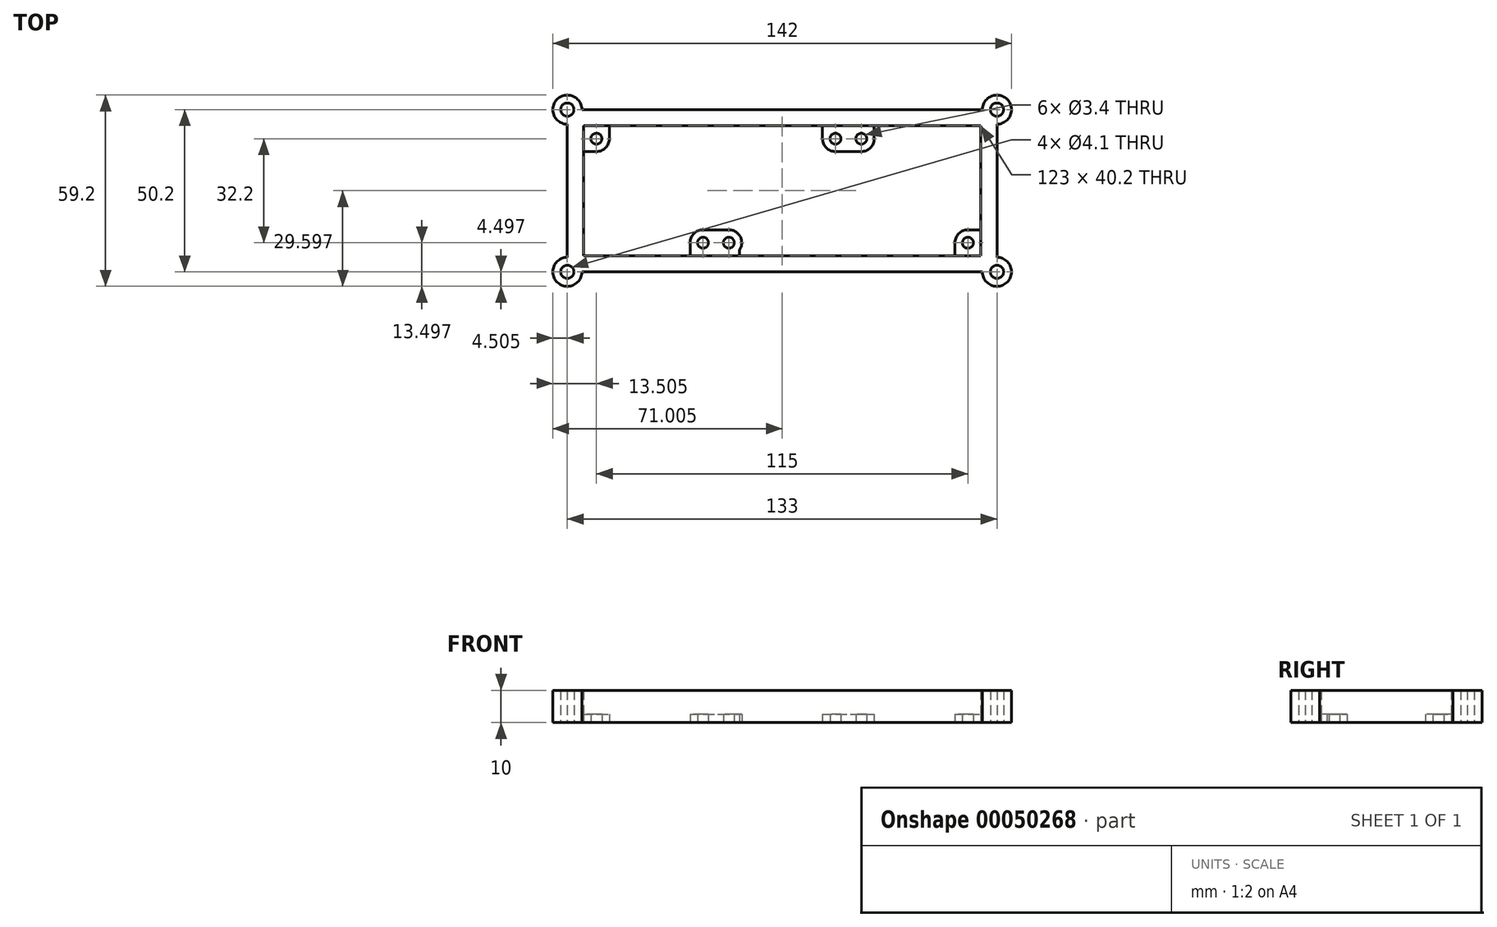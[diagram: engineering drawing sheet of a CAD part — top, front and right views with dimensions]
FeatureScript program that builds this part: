
annotation { "Feature Type Name" : "Feature", "Feature Type Description" : "" }
export const myFeature = defineFeature(function(context is Context, id is Id, definition is map)
    precondition{}
    {
        {
            var Q0;
            Q0=qCreatedBy(makeId("Top.planeOp"),FACE);
            var sketch = newSketch(context, id + "F0", { "sketchPlane" : qUnion([Q0])});
            skLineSegment(sketch, "E0.bottom", {"start": v(-53.3, 36.32) * mm, "end": v(79.7, 36.32) * mm});
            skLineSegment(sketch, "E0.top", {"start": v(-53.3, -13.88) * mm, "end": v(79.7, -13.88) * mm});
            skLineSegment(sketch, "E0.left", {"start": v(-53.3, 36.32) * mm, "end": v(-53.3, -13.88) * mm});
            skLineSegment(sketch, "E0.right", {"start": v(79.7, 36.32) * mm, "end": v(79.7, -13.88) * mm});
            skLineSegment(sketch, "E1.bottom", {"start": v(-48.3, 31.32) * mm, "end": v(74.7, 31.32) * mm});
            skLineSegment(sketch, "E1.top", {"start": v(-48.3, -8.88) * mm, "end": v(74.7, -8.88) * mm});
            skLineSegment(sketch, "E1.left", {"start": v(-48.3, 31.32) * mm, "end": v(-48.3, -8.88) * mm});
            skLineSegment(sketch, "E1.right", {"start": v(74.7, 31.32) * mm, "end": v(74.7, -8.88) * mm});
            skCircle(sketch, "E2", {"center": v(-44.3, 27.32) * mm, "radius": 4 * mm});
            skCircle(sketch, "E3", {"center": v(-3.3, -4.88) * mm, "radius": 4 * mm});
            skCircle(sketch, "E4", {"center": v(-11.3, -4.88) * mm, "radius": 4 * mm});
            skCircle(sketch, "E5", {"center": v(29.7, 27.32) * mm, "radius": 4 * mm});
            skCircle(sketch, "E6", {"center": v(37.7, 27.32) * mm, "radius": 4 * mm});
            skCircle(sketch, "E7", {"center": v(70.7, -4.88) * mm, "radius": 4 * mm});
            skLineSegment(sketch, "E8", {"start": v(29.7, 23.32) * mm, "end": v(37.7, 23.32) * mm});
            skLineSegment(sketch, "E9", {"start": v(-11.3, -0.88) * mm, "end": v(-3.3, -0.88) * mm});
            skLineSegment(sketch, "E10", {"start": v(-44.3, 23.32) * mm, "end": v(-48.3, 23.32) * mm});
            skLineSegment(sketch, "E11", {"start": v(-40.3, 27.32) * mm, "end": v(-40.3, 31.32) * mm});
            skLineSegment(sketch, "E12", {"start": v(25.7, 27.32) * mm, "end": v(25.7, 31.32) * mm});
            skLineSegment(sketch, "E13", {"start": v(41.7, 27.32) * mm, "end": v(41.7, 31.32) * mm});
            skLineSegment(sketch, "E14", {"start": v(-15.3, -4.88) * mm, "end": v(-15.3, -8.88) * mm});
            skLineSegment(sketch, "E15", {"start": v(0, -4.88) * mm, "end": v(0, -8.88) * mm});
            skLineSegment(sketch, "E16", {"start": v(66.7, -4.88) * mm, "end": v(66.7, -8.88) * mm});
            skLineSegment(sketch, "E17", {"start": v(70.7, -0.88) * mm, "end": v(74.7, -0.88) * mm});
            skCircle(sketch, "E18", {"center": v(-44.3, 27.32) * mm, "radius": 1.7 * mm});
            skCircle(sketch, "E19", {"center": v(-11.3, -4.88) * mm, "radius": 1.7 * mm});
            skCircle(sketch, "E20", {"center": v(-3.3, -4.88) * mm, "radius": 1.7 * mm});
            skCircle(sketch, "E21", {"center": v(29.7, 27.32) * mm, "radius": 1.7 * mm});
            skCircle(sketch, "E22", {"center": v(37.7, 27.32) * mm, "radius": 1.7 * mm});
            skCircle(sketch, "E23", {"center": v(70.7, -4.88) * mm, "radius": 1.7 * mm});
            skCircle(sketch, "E24", {"center": v(-53.3, 36.32) * mm, "radius": 4.5 * mm});
            skCircle(sketch, "E25", {"center": v(-53.3, -13.88) * mm, "radius": 4.5 * mm});
            skCircle(sketch, "E26", {"center": v(79.7, 36.32) * mm, "radius": 4.5 * mm});
            skCircle(sketch, "E27", {"center": v(79.7, -13.88) * mm, "radius": 4.5 * mm});
            skCircle(sketch, "E28", {"center": v(-53.3, 36.32) * mm, "radius": 2.05 * mm});
            skCircle(sketch, "E29", {"center": v(-53.3, -13.88) * mm, "radius": 2.05 * mm});
            skCircle(sketch, "E30", {"center": v(79.7, -13.88) * mm, "radius": 2.05 * mm});
            skCircle(sketch, "E31", {"center": v(79.7, 36.32) * mm, "radius": 2.05 * mm});
            skSolve(sketch);
        }
        {
            var Q0;
            {var subQ24=sQuery(id+"F0.wireOp",EDGE,"E24");var subQ38=sQuery(id+"F0.wireOp",EDGE,"E0.bottom");var subQ39=makeQuery(id+"F0.imprint","INTERSECT",VERTEX,{"derivedFrom":[subQ38,subQ24]});Q0=makeQuery(id+"F0.imprint","IMPRINT",FACE,{"disambiguationData":[TD([[makeQuery(id+"F0.imprint","IMPRINT",EDGE,{"disambiguationData":[TD([[subQ39,-1.0]])],"derivedFrom":subQ38}),-1.0]])]});}
            var Q1;
            {var subQ0=sQuery(id+"F0.wireOp",EDGE,"E24");var subQ1=sQuery(id+"F0.wireOp",EDGE,"E0.bottom");var subQ2=makeQuery(id+"F0.imprint","INTERSECT",VERTEX,{"derivedFrom":[subQ1,subQ0]});Q1=makeQuery(id+"F0.imprint","IMPRINT",FACE,{"disambiguationData":[TD([[makeQuery(id+"F0.imprint","IMPRINT",EDGE,{"disambiguationData":[TD([[subQ2,1.0]])],"derivedFrom":subQ1}),1.0]])]});}
            var Q2;
            {var subQ0=sQuery(id+"F0.wireOp",EDGE,"E24");var subQ1=sQuery(id+"F0.wireOp",EDGE,"E0.bottom");var subQ2=makeQuery(id+"F0.imprint","INTERSECT",VERTEX,{"derivedFrom":[subQ1,subQ0]});Q2=makeQuery(id+"F0.imprint","IMPRINT",FACE,{"disambiguationData":[TD([[makeQuery(id+"F0.imprint","IMPRINT",EDGE,{"disambiguationData":[TD([[subQ2,1.0]])],"derivedFrom":subQ1}),-1.0]])]});}
            var Q3;
            {var subQ0=sQuery(id+"F0.wireOp",EDGE,"E25");var subQ1=sQuery(id+"F0.wireOp",EDGE,"E0.top");var subQ2=makeQuery(id+"F0.imprint","INTERSECT",VERTEX,{"derivedFrom":[subQ1,subQ0]});Q3=makeQuery(id+"F0.imprint","IMPRINT",FACE,{"disambiguationData":[TD([[makeQuery(id+"F0.imprint","IMPRINT",EDGE,{"disambiguationData":[TD([[subQ2,1.0]])],"derivedFrom":subQ1}),-1.0]])]});}
            var Q4;
            {var subQ0=sQuery(id+"F0.wireOp",EDGE,"E25");var subQ1=sQuery(id+"F0.wireOp",EDGE,"E0.top");var subQ2=makeQuery(id+"F0.imprint","INTERSECT",VERTEX,{"derivedFrom":[subQ1,subQ0]});Q4=makeQuery(id+"F0.imprint","IMPRINT",FACE,{"disambiguationData":[TD([[makeQuery(id+"F0.imprint","IMPRINT",EDGE,{"disambiguationData":[TD([[subQ2,1.0]])],"derivedFrom":subQ1}),1.0]])]});}
            var Q5;
            {var subQ0=sQuery(id+"F0.wireOp",EDGE,"E27");var subQ1=sQuery(id+"F0.wireOp",EDGE,"E0.top");var subQ2=makeQuery(id+"F0.imprint","INTERSECT",VERTEX,{"derivedFrom":[subQ1,subQ0]});Q5=makeQuery(id+"F0.imprint","IMPRINT",FACE,{"disambiguationData":[TD([[makeQuery(id+"F0.imprint","IMPRINT",EDGE,{"disambiguationData":[TD([[subQ2,-1.0]])],"derivedFrom":subQ1}),-1.0]])]});}
            var Q6;
            {var subQ0=sQuery(id+"F0.wireOp",EDGE,"E27");var subQ1=sQuery(id+"F0.wireOp",EDGE,"E0.top");var subQ2=makeQuery(id+"F0.imprint","INTERSECT",VERTEX,{"derivedFrom":[subQ1,subQ0]});Q6=makeQuery(id+"F0.imprint","IMPRINT",FACE,{"disambiguationData":[TD([[makeQuery(id+"F0.imprint","IMPRINT",EDGE,{"disambiguationData":[TD([[subQ2,-1.0]])],"derivedFrom":subQ1}),1.0]])]});}
            var Q7;
            {var subQ0=sQuery(id+"F0.wireOp",EDGE,"E26");var subQ1=sQuery(id+"F0.wireOp",EDGE,"E0.bottom");var subQ2=makeQuery(id+"F0.imprint","INTERSECT",VERTEX,{"derivedFrom":[subQ1,subQ0]});Q7=makeQuery(id+"F0.imprint","IMPRINT",FACE,{"disambiguationData":[TD([[makeQuery(id+"F0.imprint","IMPRINT",EDGE,{"disambiguationData":[TD([[subQ2,-1.0]])],"derivedFrom":subQ1}),-1.0]])]});}
            var Q8;
            {var subQ0=sQuery(id+"F0.wireOp",EDGE,"E26");var subQ1=sQuery(id+"F0.wireOp",EDGE,"E0.bottom");var subQ2=makeQuery(id+"F0.imprint","INTERSECT",VERTEX,{"derivedFrom":[subQ1,subQ0]});Q8=makeQuery(id+"F0.imprint","IMPRINT",FACE,{"disambiguationData":[TD([[makeQuery(id+"F0.imprint","IMPRINT",EDGE,{"disambiguationData":[TD([[subQ2,-1.0]])],"derivedFrom":subQ1}),1.0]])]});}
            extrude(context, id + "F1", {"entities" : qUnion([Q0, Q1, Q2, Q3, Q4, Q5, Q6, Q7, Q8]), "depth" : 10 * mm});
        }
        {
            var Q0;
            {var subQ0=sQuery(id+"F0.wireOp",EDGE,"E11");Q0=makeQuery(id+"F0.imprint","IMPRINT",FACE,{"disambiguationData":[TD([[makeQuery(id+"F0.imprint","IMPRINT",EDGE,{"derivedFrom":subQ0}),1.0]])]});}
            var Q1;
            {var subQ0=sQuery(id+"F0.wireOp",EDGE,"E1.left");var subQ1=sQuery(id+"F0.wireOp",EDGE,"E1.bottom");var subQ2=makeQuery(id+"F0.imprint","INTERSECT",VERTEX,{"derivedFrom":[subQ1,subQ0]});Q1=makeQuery(id+"F0.imprint","IMPRINT",FACE,{"disambiguationData":[TD([[makeQuery(id+"F0.imprint","IMPRINT",EDGE,{"disambiguationData":[TD([[subQ2,-1.0]])],"derivedFrom":subQ1}),-1.0]])]});}
            var Q2;
            {var subQ0=sQuery(id+"F0.wireOp",EDGE,"E10");Q2=makeQuery(id+"F0.imprint","IMPRINT",FACE,{"disambiguationData":[TD([[makeQuery(id+"F0.imprint","IMPRINT",EDGE,{"derivedFrom":subQ0}),-1.0]])]});}
            var Q3;
            Q3=makeQuery(id+"F0.imprint","IMPRINT",FACE,{"disambiguationData":[TD([[makeQuery(id+"F0.imprint","IMPRINT",EDGE,{"derivedFrom":sQuery(id+"F0.wireOp",EDGE,"E18")}),-1.0]])]});
            var Q4;
            {var subQ0=sQuery(id+"F0.wireOp",EDGE,"E9");Q4=makeQuery(id+"F0.imprint","IMPRINT",FACE,{"disambiguationData":[TD([[makeQuery(id+"F0.imprint","IMPRINT",EDGE,{"derivedFrom":subQ0}),-1.0]])]});}
            var Q5;
            Q5=makeQuery(id+"F0.imprint","IMPRINT",FACE,{"disambiguationData":[TD([[makeQuery(id+"F0.imprint","IMPRINT",EDGE,{"derivedFrom":sQuery(id+"F0.wireOp",EDGE,"E19")}),-1.0]])]});
            var Q6;
            Q6=makeQuery(id+"F0.imprint","IMPRINT",FACE,{"disambiguationData":[TD([[makeQuery(id+"F0.imprint","IMPRINT",EDGE,{"derivedFrom":sQuery(id+"F0.wireOp",EDGE,"E20")}),-1.0]])]});
            var Q7;
            {var subQ0=sQuery(id+"F0.wireOp",EDGE,"E4");var subQ1=sQuery(id+"F0.wireOp",EDGE,"E1.top");var subQ2=makeQuery(id+"F0.imprint","INTERSECT",VERTEX,{"derivedFrom":[subQ1,subQ0]});Q7=makeQuery(id+"F0.imprint","IMPRINT",FACE,{"disambiguationData":[TD([[makeQuery(id+"F0.imprint","IMPRINT",EDGE,{"disambiguationData":[TD([[subQ2,-1.0]])],"derivedFrom":subQ1}),1.0]])]});}
            var Q8;
            {var subQ0=sQuery(id+"F0.wireOp",EDGE,"E15");var subQ1=sQuery(id+"F0.wireOp",EDGE,"E1.top");var subQ2=makeQuery(id+"F0.imprint","INTERSECT",VERTEX,{"derivedFrom":[subQ1,subQ0]});Q8=makeQuery(id+"F0.imprint","IMPRINT",FACE,{"disambiguationData":[TD([[makeQuery(id+"F0.imprint","IMPRINT",EDGE,{"disambiguationData":[TD([[subQ2,1.0]])],"derivedFrom":subQ1}),1.0]])]});}
            var Q9;
            {var subQ0=sQuery(id+"F0.wireOp",EDGE,"E14");Q9=makeQuery(id+"F0.imprint","IMPRINT",FACE,{"disambiguationData":[TD([[makeQuery(id+"F0.imprint","IMPRINT",EDGE,{"derivedFrom":subQ0}),1.0]])]});}
            var Q10;
            {var subQ0=sQuery(id+"F0.wireOp",EDGE,"E4");var subQ1=sQuery(id+"F0.wireOp",EDGE,"E3");var subQ2=makeQuery(id+"F0.imprint","INTERSECT",VERTEX,{"disambiguationData":[OD(0.0)],"derivedFrom":[subQ1,subQ0]});Q10=makeQuery(id+"F0.imprint","IMPRINT",FACE,{"disambiguationData":[TD([[makeQuery(id+"F0.imprint","IMPRINT",EDGE,{"disambiguationData":[TD([[subQ2,-1.0]])],"derivedFrom":subQ1}),1.0]])]});}
            var Q11;
            Q11=makeQuery(id+"F0.imprint","IMPRINT",FACE,{"disambiguationData":[TD([[makeQuery(id+"F0.imprint","IMPRINT",EDGE,{"derivedFrom":sQuery(id+"F0.wireOp",EDGE,"E22")}),-1.0]])]});
            var Q12;
            {var subQ0=sQuery(id+"F0.wireOp",EDGE,"E12");Q12=makeQuery(id+"F0.imprint","IMPRINT",FACE,{"disambiguationData":[TD([[makeQuery(id+"F0.imprint","IMPRINT",EDGE,{"derivedFrom":subQ0}),-1.0]])]});}
            var Q13;
            {var subQ0=sQuery(id+"F0.wireOp",EDGE,"E8");Q13=makeQuery(id+"F0.imprint","IMPRINT",FACE,{"disambiguationData":[TD([[makeQuery(id+"F0.imprint","IMPRINT",EDGE,{"derivedFrom":subQ0}),1.0]])]});}
            var Q14;
            {var subQ0=sQuery(id+"F0.wireOp",EDGE,"E13");Q14=makeQuery(id+"F0.imprint","IMPRINT",FACE,{"disambiguationData":[TD([[makeQuery(id+"F0.imprint","IMPRINT",EDGE,{"derivedFrom":subQ0}),1.0]])]});}
            var Q15;
            {var subQ0=sQuery(id+"F0.wireOp",EDGE,"E5");var subQ1=sQuery(id+"F0.wireOp",EDGE,"E1.bottom");var subQ2=makeQuery(id+"F0.imprint","INTERSECT",VERTEX,{"derivedFrom":[subQ1,subQ0]});Q15=makeQuery(id+"F0.imprint","IMPRINT",FACE,{"disambiguationData":[TD([[makeQuery(id+"F0.imprint","IMPRINT",EDGE,{"disambiguationData":[TD([[subQ2,-1.0]])],"derivedFrom":subQ1}),-1.0]])]});}
            var Q16;
            Q16=makeQuery(id+"F0.imprint","IMPRINT",FACE,{"disambiguationData":[TD([[makeQuery(id+"F0.imprint","IMPRINT",EDGE,{"derivedFrom":sQuery(id+"F0.wireOp",EDGE,"E21")}),-1.0]])]});
            var Q17;
            {var subQ0=sQuery(id+"F0.wireOp",EDGE,"E6");var subQ1=sQuery(id+"F0.wireOp",EDGE,"E5");var subQ2=makeQuery(id+"F0.imprint","INTERSECT",VERTEX,{"disambiguationData":[OD(0.0)],"derivedFrom":[subQ1,subQ0]});Q17=makeQuery(id+"F0.imprint","IMPRINT",FACE,{"disambiguationData":[TD([[makeQuery(id+"F0.imprint","IMPRINT",EDGE,{"disambiguationData":[TD([[subQ2,1.0]])],"derivedFrom":subQ1}),1.0]])]});}
            var Q18;
            Q18=makeQuery(id+"F0.imprint","IMPRINT",FACE,{"disambiguationData":[TD([[makeQuery(id+"F0.imprint","IMPRINT",EDGE,{"derivedFrom":sQuery(id+"F0.wireOp",EDGE,"E23")}),-1.0]])]});
            var Q19;
            {var subQ0=sQuery(id+"F0.wireOp",EDGE,"E16");Q19=makeQuery(id+"F0.imprint","IMPRINT",FACE,{"disambiguationData":[TD([[makeQuery(id+"F0.imprint","IMPRINT",EDGE,{"derivedFrom":subQ0}),1.0]])]});}
            var Q20;
            {var subQ0=sQuery(id+"F0.wireOp",EDGE,"E17");Q20=makeQuery(id+"F0.imprint","IMPRINT",FACE,{"disambiguationData":[TD([[makeQuery(id+"F0.imprint","IMPRINT",EDGE,{"derivedFrom":subQ0}),-1.0]])]});}
            var Q21;
            {var subQ0=sQuery(id+"F0.wireOp",EDGE,"E1.right");var subQ1=sQuery(id+"F0.wireOp",EDGE,"E1.top");var subQ2=makeQuery(id+"F0.imprint","INTERSECT",VERTEX,{"derivedFrom":[subQ1,subQ0]});Q21=makeQuery(id+"F0.imprint","IMPRINT",FACE,{"disambiguationData":[TD([[makeQuery(id+"F0.imprint","IMPRINT",EDGE,{"disambiguationData":[TD([[subQ2,1.0]])],"derivedFrom":subQ1}),1.0]])]});}
            extrude(context, id + "F2", {"entities" : qUnion([Q0, Q1, Q2, Q3, Q4, Q5, Q6, Q7, Q8, Q9, Q10, Q11, Q12, Q13, Q14, Q15, Q16, Q17, Q18, Q19, Q20, Q21]), "operationType" : NewBodyOperationType.ADD, "depth" : 2.6 * mm});
        }
    });
